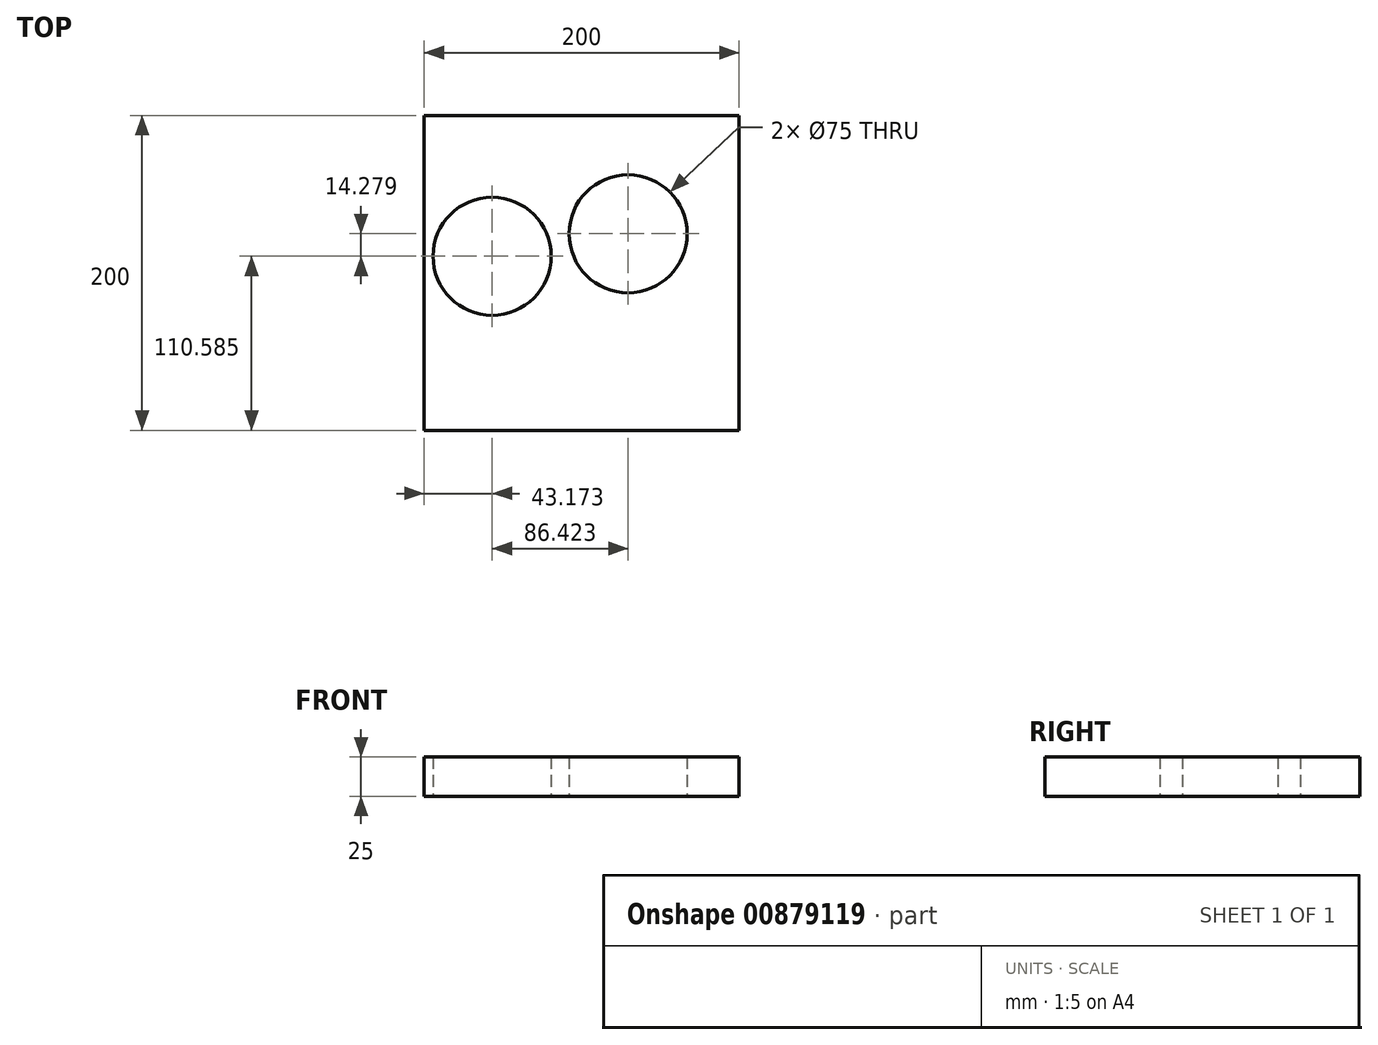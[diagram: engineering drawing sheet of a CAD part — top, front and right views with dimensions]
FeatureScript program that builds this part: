
annotation { "Feature Type Name" : "Feature", "Feature Type Description" : "" }
export const myFeature = defineFeature(function(context is Context, id is Id, definition is map)
    precondition{}
    {
        {
            var Q0;
            Q0=qCreatedBy(makeId("Top.planeOp"),FACE);
            var sketch = newSketch(context, id + "F0", { "sketchPlane" : qUnion([Q0])});
            skLineSegment(sketch, "E0.bottom", {"start": v(-150.04, 193.9) * mm, "end": v(49.96, 193.9) * mm});
            skLineSegment(sketch, "E0.top", {"start": v(-150.04, -6.1) * mm, "end": v(49.96, -6.1) * mm});
            skLineSegment(sketch, "E0.left", {"start": v(-150.04, 193.9) * mm, "end": v(-150.04, -6.1) * mm});
            skLineSegment(sketch, "E0.right", {"start": v(49.96, 193.9) * mm, "end": v(49.96, -6.1) * mm});
            skCircle(sketch, "E1", {"center": v(-106.87, 104.48) * mm, "radius": 37.5 * mm});
            skCircle(sketch, "E2", {"center": v(-20.44, 118.75) * mm, "radius": 37.5 * mm});
            skSolve(sketch);
        }
        {
            var Q0;
            Q0 = qSketchRegion(id + "F0", true);
            extrude(context, id + "F1", {"entities" : qUnion([Q0]), "depth" : 25 * mm, "offsetDistance" : 25 * mm});
        }
    });
